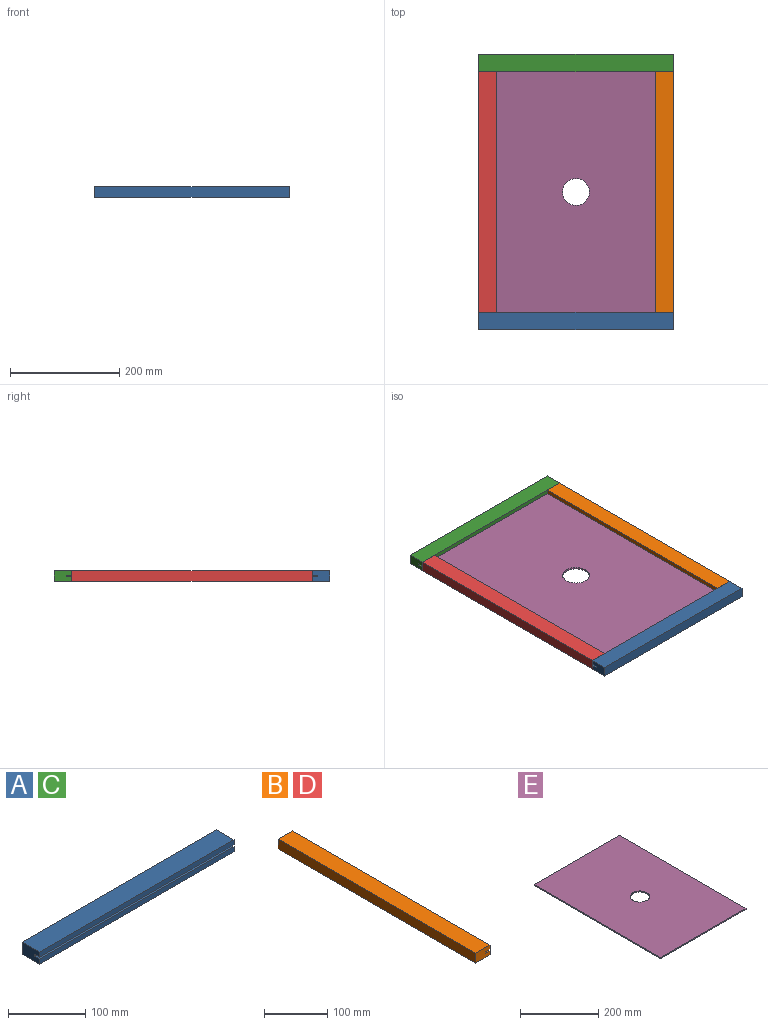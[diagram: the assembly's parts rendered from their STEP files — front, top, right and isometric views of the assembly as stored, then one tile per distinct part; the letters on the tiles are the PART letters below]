
ASSEMBLY  parts=5 mates=4
PART A: 10 faces, bbox 355.6x31.8x19.1 mm
  f0: plane 355.6x7.94mm, normal (0,-1,0), area 2822.6mm2, adj f1,f3,f4,f7
  f1: plane 31.75x19.05mm, normal (-1,0,0), area 574.6mm2, adj f0,f2,f4,f5,f6,f7,f8,f9
  f2: plane 355.6x31.75mm, normal (0,0,-1), area 11290.3mm2, adj f1,f3,f5,f6
  f3: plane 31.75x19.05mm, normal (1,0,0), area 574.6mm2, adj f0,f2,f4,f5,f6,f7,f8,f9
  f4: plane 355.6x31.75mm, normal (0,0,1), area 11290.3mm2, adj f0,f1,f3,f5
  f5: plane 355.6x19.05mm, normal (0,1,0), area 6774.2mm2, adj f1,f2,f3,f4
  f6: plane 355.6x7.94mm, normal (0,-1,0), area 2822.6mm2, adj f1,f2,f3,f8
  f7: plane 355.6x9.53mm, normal (0,0,-1), area 3387.1mm2, adj f0,f1,f3,f9
  f8: plane 355.6x9.53mm, normal (0,0,1), area 3387.1mm2, adj f1,f3,f6,f9
  f9: plane 355.6x3.18mm, normal (0,-1,0), area 1129mm2, adj f1,f3,f7,f8
PART B: 10 faces, bbox 31.8x441.3x19.1 mm
  f0: plane 441.33x19.05mm, normal (-1,0,0), area 8407.2mm2, adj f1,f7,f8,f9
  f1: plane 441.33x31.75mm, normal (0,0,-1), area 14012.1mm2, adj f0,f2,f8,f9
  f2: plane 441.33x7.94mm, normal (1,0,0), area 3503mm2, adj f1,f3,f8,f9
  f3: plane 441.33x9.53mm, normal (0,0,1), area 4203.6mm2, adj f2,f4,f8,f9
  f4: plane 441.33x3.18mm, normal (1,0,0), area 1401.2mm2, adj f3,f5,f8,f9
  f5: plane 441.33x9.53mm, normal (0,0,-1), area 4203.6mm2, adj f4,f6,f8,f9
  f6: plane 441.33x7.94mm, normal (1,0,0), area 3503mm2, adj f5,f7,f8,f9
  f7: plane 441.33x31.75mm, normal (0,0,1), area 14012.1mm2, adj f0,f6,f8,f9
  f8: plane 31.75x19.05mm, normal (0,-1,0), area 574.6mm2, adj f0,f1,f2,f3,f4,f5,f6,f7
  f9: plane 31.75x19.05mm, normal (0,1,0), area 574.6mm2, adj f0,f1,f2,f3,f4,f5,f6,f7
PART C: same geometry as A
PART D: same geometry as B
PART E: 7 faces, bbox 308x457.2x3.2 mm
  f0: plane 307.98x3.18mm, normal (0,-1,0), area 977.8mm2, adj f1,f4,f5,f6
  f1: plane 457.2x3.18mm, normal (1,0,0), area 1451.6mm2, adj f0,f2,f5,f6
  f2: plane 307.98x3.18mm, normal (0,1,0), area 977.8mm2, adj f1,f4,f5,f6
  f3: cylinder r=24.61mm len=49.21mm, axis (0,0,1), area 490.9mm2, adj f5,f6
  f4: plane 457.2x3.18mm, normal (-1,0,0), area 1451.6mm2, adj f0,f2,f5,f6
  f5: plane 457.2x307.98mm, normal (0,0,1), area 138904mm2, adj f0,f1,f2,f3,f4
  f6: plane 457.2x307.98mm, normal (0,0,-1), area 138904mm2, adj f0,f1,f2,f3,f4
PLACE A rot(axis=(0,0,1),180deg) t=(0,-441.33,0)mm
PLACE B rot(axis=(0,0,1),180deg) t=(-25.4,-441.33,0)mm
PLACE C at identity fixed
PLACE D t=(25.4,0,0)mm
PLACE E t=(0,-1.59,0)mm
MATE fastened D.f7 <-> C.f4  axis (0,0,1) through (-177.8,0,9.53)mm
MATE fastened C.f4 <-> B.f7  axis (0,0,1) through (177.8,0,9.53)mm
MATE fastened C.f8 <-> E.f6  axis (0,0,1) through (0,9.52,-1.59)mm
MATE fastened A.f4 <-> D.f7  axis (0,0,1) through (-177.8,-441.33,9.53)mm
